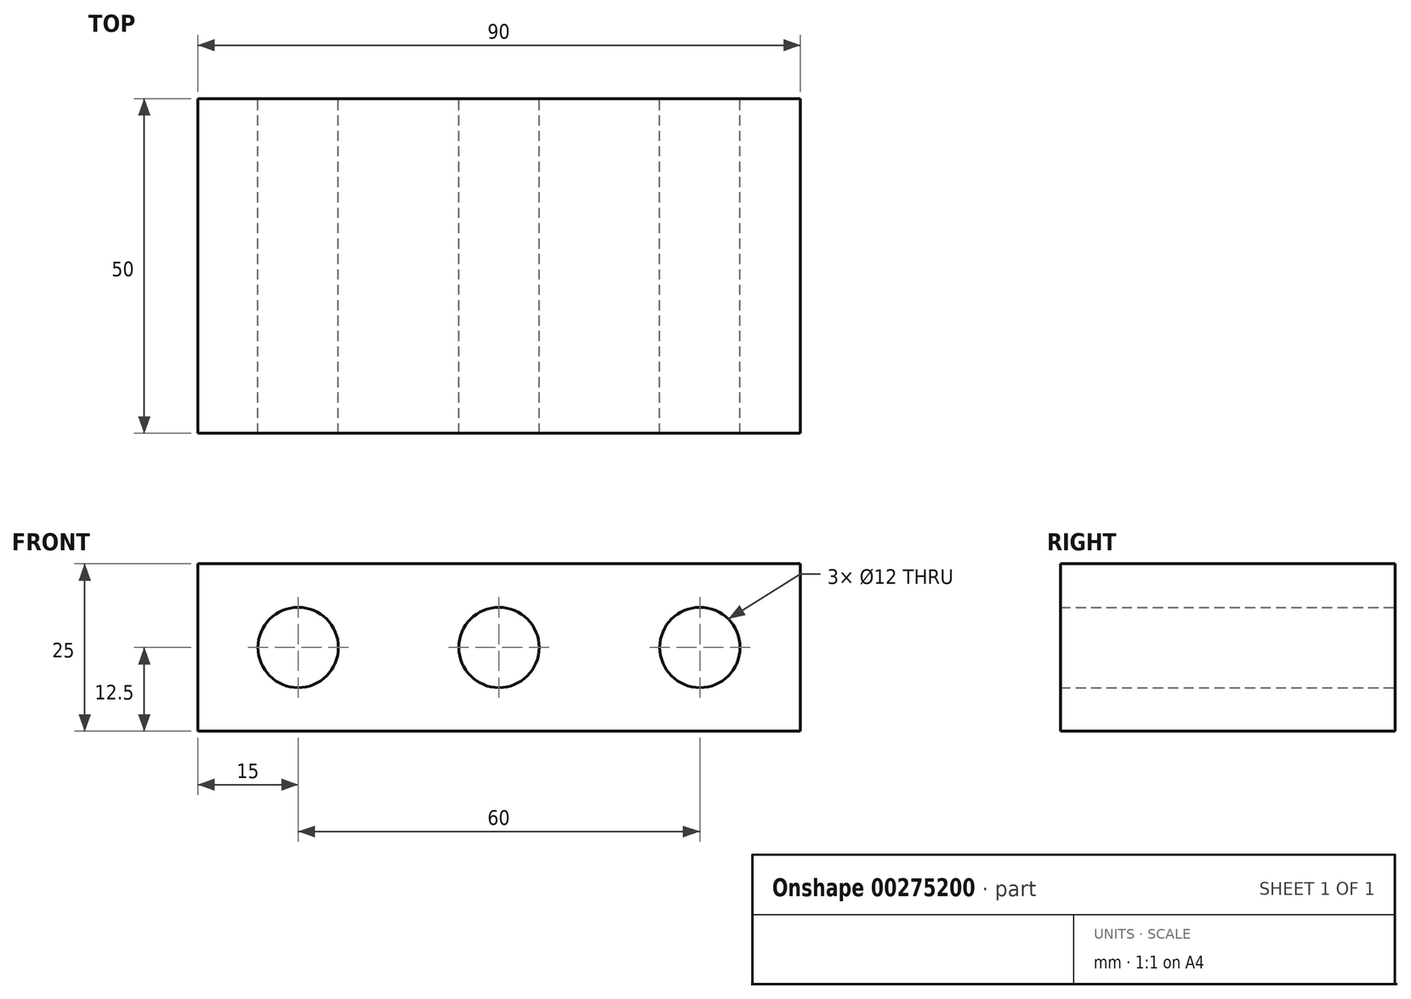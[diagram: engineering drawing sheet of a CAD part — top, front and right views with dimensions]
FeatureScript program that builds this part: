
annotation { "Feature Type Name" : "Feature", "Feature Type Description" : "" }
export const myFeature = defineFeature(function(context is Context, id is Id, definition is map)
    precondition{}
    {
        {
            var Q0;
            Q0=qCreatedBy(makeId("Front.planeOp"),FACE);
            var sketch = newSketch(context, id + "F0", { "sketchPlane" : qUnion([Q0])});
            skLineSegment(sketch, "E0.bottom", {"start": v(45, 12.5) * mm, "end": v(-45, 12.5) * mm});
            skLineSegment(sketch, "E0.top", {"start": v(45, -12.5) * mm, "end": v(-45, -12.5) * mm});
            skLineSegment(sketch, "E0.left", {"start": v(45, 12.5) * mm, "end": v(45, -12.5) * mm});
            skLineSegment(sketch, "E0.right", {"start": v(-45, 12.5) * mm, "end": v(-45, -12.5) * mm});
            skPoint(sketch, "E0.middle", {"position": v(0, 0) * mm});
            skCircle(sketch, "E1", {"center": v(-30, 0) * mm, "radius": 6 * mm});
            skLineSegment(sketch, "E2", {"start": v(0, 12.5) * mm, "end": v(0, -12.5) * mm, "construction": true});
            skLineSegment(sketch, "E3", {"start": v(-45, 0) * mm, "end": v(45, 0) * mm, "construction": true});
            skCircle(sketch, "E4.MirrorC", {"center": v(30, 0) * mm, "radius": 6 * mm});
            skCircle(sketch, "E5", {"center": v(0, 0) * mm, "radius": 6 * mm});
            skSolve(sketch);
        }
        {
            var Q0;
            Q0=makeQuery(id+"F0.imprint","IMPRINT",FACE,{"disambiguationData":[TD([[makeQuery(id+"F0.imprint","IMPRINT",EDGE,{"derivedFrom":sQuery(id+"F0.wireOp",EDGE,"E0.bottom")}),1.0]])]});
            extrude(context, id + "F1", {"entities" : qUnion([Q0]), "depth" : 50 * mm, "offsetDistance" : 25 * mm});
        }
    });
